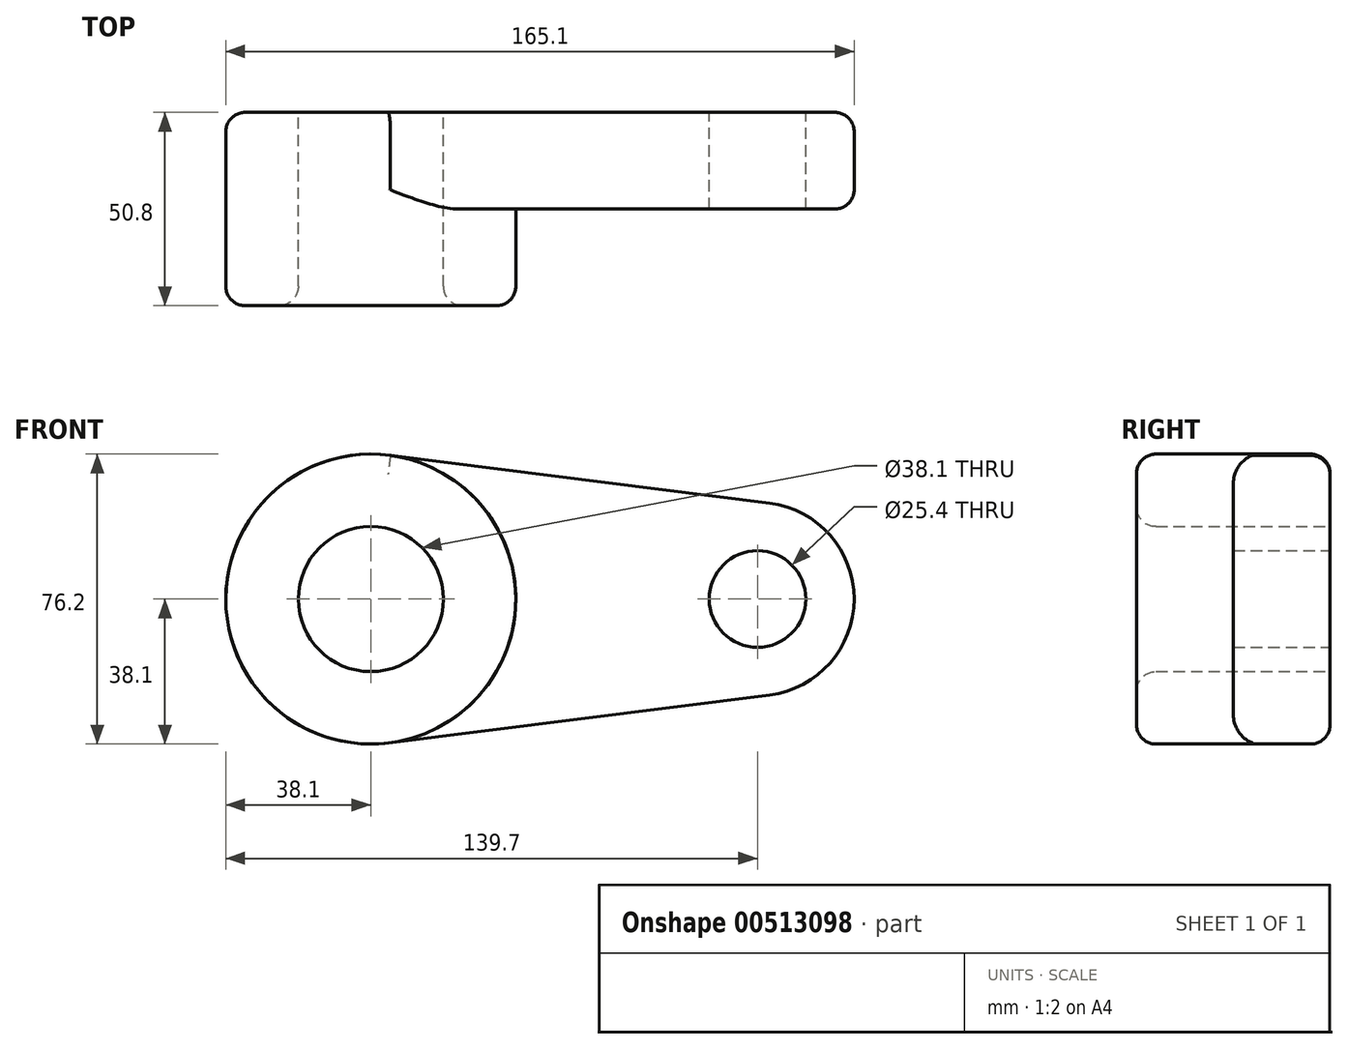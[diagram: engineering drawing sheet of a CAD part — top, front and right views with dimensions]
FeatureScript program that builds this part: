
annotation { "Feature Type Name" : "Feature", "Feature Type Description" : "" }
export const myFeature = defineFeature(function(context is Context, id is Id, definition is map)
    precondition{}
    {
        {
            var Q0;
            Q0=qCreatedBy(makeId("Front.planeOp"),FACE);
            var sketch = newSketch(context, id + "F0", { "sketchPlane" : qUnion([Q0])});
            skCircle(sketch, "E0", {"center": v(0, 0) * mm, "radius": 38.1 * mm});
            skCircle(sketch, "E1", {"center": v(101.6, 0) * mm, "radius": 25.4 * mm});
            skLineSegment(sketch, "E2", {"start": v(5.16, 37.75) * mm, "end": v(104.77, 25.2) * mm});
            skLineSegment(sketch, "E3", {"start": v(4.76, -37.8) * mm, "end": v(104.78, -25.2) * mm});
            skCircle(sketch, "E4", {"center": v(0, 0) * mm, "radius": 19.05 * mm});
            skCircle(sketch, "E5", {"center": v(101.6, 0) * mm, "radius": 12.7 * mm});
            skSolve(sketch);
        }
        {
            var Q0;
            Q0 = qSketchRegion(id + "F0", true);
            extrude(context, id + "F1", {"entities" : qUnion([Q0]), "depth" : 25.4 * mm, "offsetDistance" : 25.4 * mm});
        }
        {
            var Q0;
            Q0=makeQuery(id+"F0.imprint","IMPRINT",FACE,{"disambiguationData":[TD([[makeQuery(id+"F0.imprint","IMPRINT",EDGE,{"derivedFrom":sQuery(id+"F0.wireOp",EDGE,"E4")}),-1.0]])]});
            extrude(context, id + "F2", {"entities" : qUnion([Q0]), "operationType" : NewBodyOperationType.ADD, "depth" : 50.8 * mm, "offsetDistance" : 25.4 * mm});
        }
        {
            var Q0;
            Q0=makeQuery(id+"F2.opExtrude","CAP_FACE",FACE,{"disambiguationData":[OSD([sQuery(id+"F0.wireOp",EDGE,"E0"),sQuery(id+"F0.wireOp",EDGE,"E4")])],"isStart":false});
            var Q1;
            Q1=makeQuery(id+"F1.opExtrude","SWEPT_FACE",FACE,{"disambiguationData":[OSD([sQuery(id+"F0.wireOp",EDGE,"E3")])]});
            fillet(context, id + "F3", {"entities" : qUnion([Q0, Q1]), "radius" : 5.08 * mm, "tangentPropagation" : true, "allowEdgeOverflow" : false});
        }
    });
